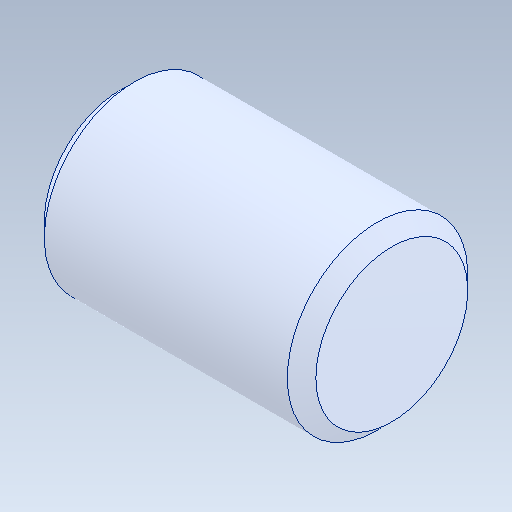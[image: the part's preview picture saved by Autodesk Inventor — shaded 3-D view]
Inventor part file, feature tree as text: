
AUTODESK INVENTOR PART (.ipt)
format: ipt  version: 2020 (Build 240168000, 168)  size: 103,936 bytes
history: native  units: in
note: dims shown in document units (in); Inventor stores cm internally (conversion verified against a paired STEP export)
features: chamfer x1
ambient origin geometry x8: Origin, YZ Plane, XZ Plane, XY Plane, X Axis, Y Axis, Z Axis, Center Point
bodies: Solid1 (feature_tree)
feature tree (1):
  chamfer  "Chamfer1"  [1 undecoded]
note: 1 required parameter value undecoded (feature->parameter linkage not recoverable at this tier; creation-order binding heuristic only, values carry confidence <= 0.55)
